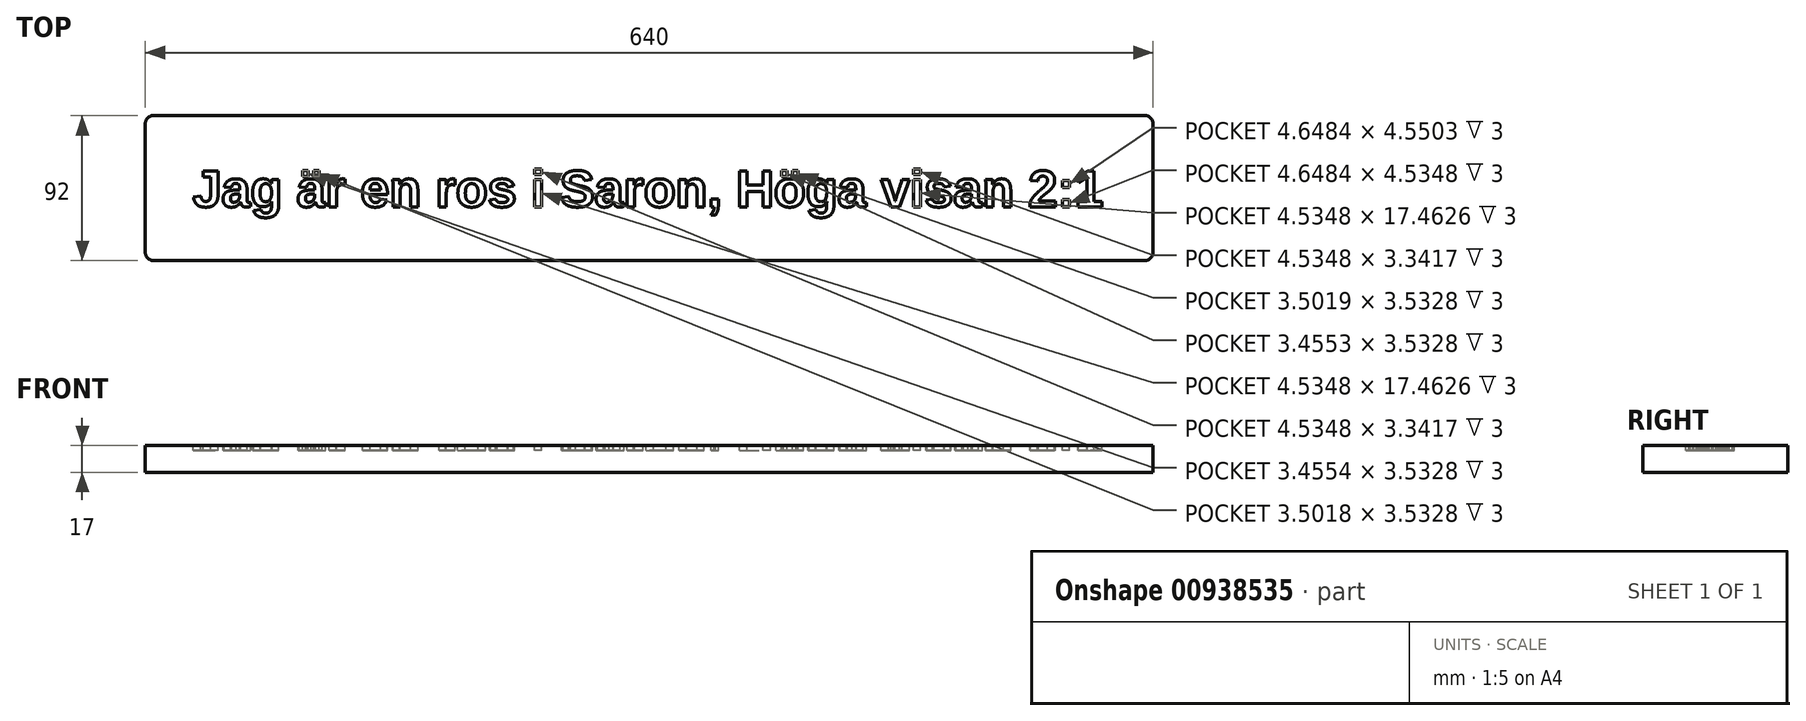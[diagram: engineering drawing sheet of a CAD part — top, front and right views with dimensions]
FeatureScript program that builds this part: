
annotation { "Feature Type Name" : "Feature", "Feature Type Description" : "" }
export const myFeature = defineFeature(function(context is Context, id is Id, definition is map)
    precondition{}
    {
        {
            var Q0;
            Q0=qCreatedBy(makeId("Top.planeOp"),FACE);
            var sketch = newSketch(context, id + "F0", { "sketchPlane" : qUnion([Q0])});
            skLineSegment(sketch, "E0.bottom", {"start": v(-627.84, 74.97) * mm, "end": v(2.16, 74.97) * mm});
            skLineSegment(sketch, "E0.top", {"start": v(-627.84, -17.03) * mm, "end": v(2.16, -17.03) * mm});
            skLineSegment(sketch, "E0.left", {"start": v(-632.84, 69.97) * mm, "end": v(-632.84, -12.03) * mm});
            skLineSegment(sketch, "E0.right", {"start": v(7.16, 69.97) * mm, "end": v(7.16, -12.03) * mm});
            skPoint(sketch, "E1.visualSharp", {"position": v(-632.84, 74.97) * mm});
            skArc(sketch, "E1.filletArc", {"start": v(-627.84, 74.97) * mm, "mid": v(-631.37, 73.51) * mm, "end": v(-632.84, 69.97) * mm});
            skPoint(sketch, "E2.visualSharp", {"position": v(-632.84, -17.03) * mm});
            skArc(sketch, "E2.filletArc", {"start": v(-632.84, -12.03) * mm, "mid": v(-631.37, -15.56) * mm, "end": v(-627.84, -17.03) * mm});
            skPoint(sketch, "E3.visualSharp", {"position": v(7.16, 74.97) * mm});
            skArc(sketch, "E3.filletArc", {"start": v(7.16, 69.97) * mm, "mid": v(5.7, 73.51) * mm, "end": v(2.16, 74.97) * mm});
            skPoint(sketch, "E4.visualSharp", {"position": v(7.16, -17.03) * mm});
            skArc(sketch, "E4.filletArc", {"start": v(2.16, -17.03) * mm, "mid": v(5.7, -15.56) * mm, "end": v(7.16, -12.03) * mm});
            skSolve(sketch);
        }
        {
            var Q0;
            Q0 = qSketchRegion(id + "F0", true);
            extrude(context, id + "F1", {"entities" : qUnion([Q0]), "depth" : 17 * mm, "offsetDistance" : 25 * mm});
        }
        {
            var Q0;
            Q0=makeQuery(id+"F1.opExtrude","CAP_FACE",FACE,{"disambiguationData":[OSD([sQuery(id+"F0.wireOp",EDGE,"E0.bottom"),sQuery(id+"F0.wireOp",EDGE,"E0.top"),sQuery(id+"F0.wireOp",EDGE,"E0.left"),sQuery(id+"F0.wireOp",EDGE,"E0.right")])],"isStart":false});
            var sketch = newSketch(context, id + "F2", { "sketchPlane" : qUnion([Q0])});
            skPoint(sketch, "E5.firstSnap0", {"position": v(-131.57, 11.72) * mm});
            skText(sketch, "E6", { "text": "Jag är en ros i Saron, Höga visan 2:1", "fontName": "Arimo-Bold.ttf"});
            skLineSegment(sketch, "E7", {"start": v(-312.84, 74.97) * mm, "end": v(-312.84, -17.03) * mm, "construction": true});
            skPoint(sketch, "E8.startSnap0", {"position": v(-22.84, 28.97) * mm});
            skPoint(sketch, "E8.endSnap0", {"position": v(-632.84, 28.97) * mm});
            skLineSegment(sketch, "E9", {"start": v(-632.84, 28.97) * mm, "end": v(7.16, 28.97) * mm, "construction": true});
            const initialGuessF2  = {"E6": [-0.60284, 0.01708, 1, 0, 0.0238]};
            skSetInitialGuess(sketch, initialGuessF2);
            skSolve(sketch);
        }
        {
            var Q0;
            Q0 = qSketchRegion(id + "F2", true);
            extrude(context, id + "F3", {"entities" : qUnion([Q0]), "operationType" : NewBodyOperationType.REMOVE, "oppositeDirection" : true, "depth" : 3 * mm, "offsetDistance" : 25 * mm});
        }
    });
